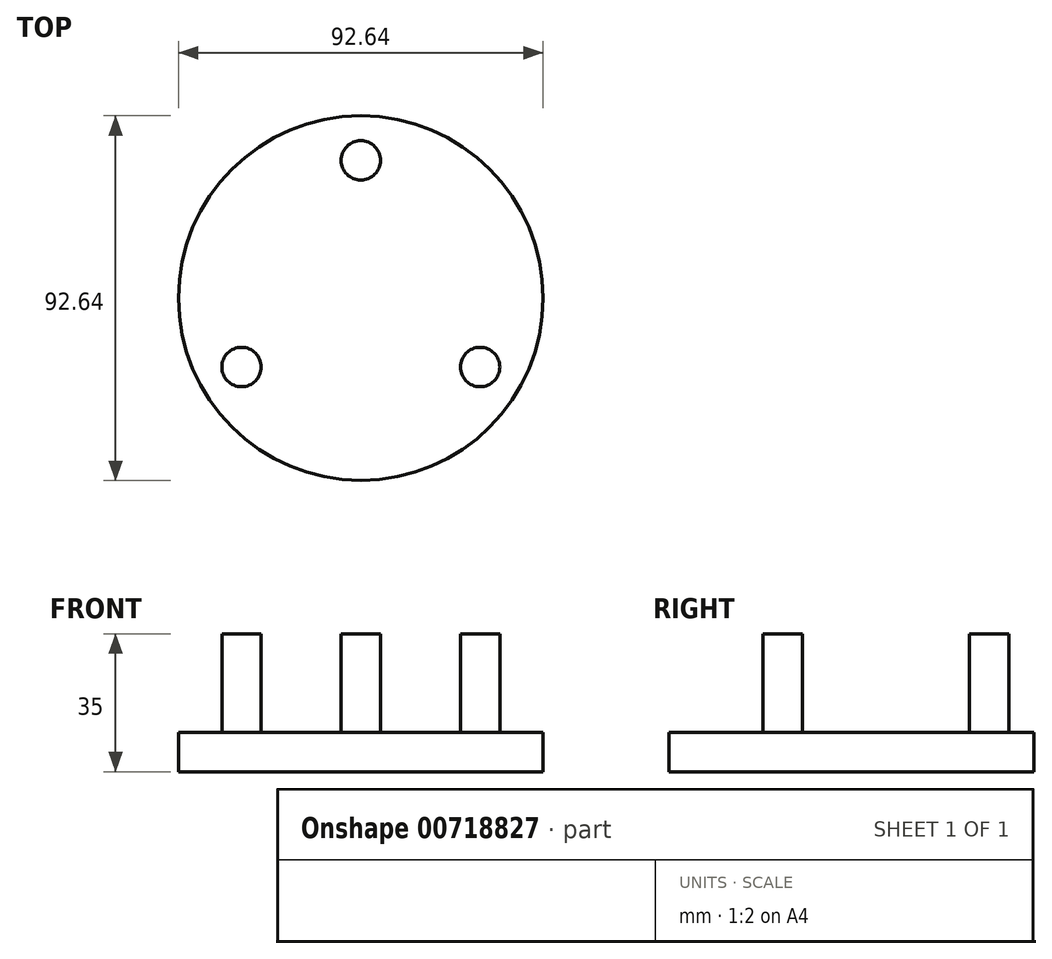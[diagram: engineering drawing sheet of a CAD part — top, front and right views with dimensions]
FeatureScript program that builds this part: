
annotation { "Feature Type Name" : "Feature", "Feature Type Description" : "" }
export const myFeature = defineFeature(function(context is Context, id is Id, definition is map)
    precondition{}
    {
        {
            var Q0;
            Q0=qCreatedBy(makeId("Top.planeOp"),FACE);
            var sketch = newSketch(context, id + "F0", { "sketchPlane" : qUnion([Q0])});
            skCircle(sketch, "E0", {"center": v(0, 0) * mm, "radius": 46.32 * mm});
            skSolve(sketch);
        }
        {
            var Q0;
            Q0=makeQuery(id+"F0.imprint","IMPRINT",FACE,{"disambiguationData":[TD([[makeQuery(id+"F0.imprint","IMPRINT",EDGE,{"derivedFrom":sQuery(id+"F0.wireOp",EDGE,"E0")}),1.0]])]});
            extrude(context, id + "F1", {"entities" : qUnion([Q0]), "endBound" : BoundingType.SYMMETRIC, "depth" : 10 * mm, "offsetDistance" : 25 * mm});
        }
        {
            var Q0;
            Q0=makeQuery(id+"F1.opExtrude","CAP_FACE",FACE,{"disambiguationData":[OSD([sQuery(id+"F0.wireOp",EDGE,"E0")])],"isStart":false});
            var sketch = newSketch(context, id + "F2", { "sketchPlane" : qUnion([Q0])});
            skCircle(sketch, "E1", {"center": v(0, 35) * mm, "radius": 5 * mm});
            skPoint(sketch, "E2.center", {"position": v(0, 0) * mm});
            skLineSegment(sketch, "E2.anchor1", {"start": v(0, 0) * mm, "end": v(0, 35) * mm, "construction": true});
            skLineSegment(sketch, "E2.anchor2", {"start": v(0, 0) * mm, "end": v(0, 35) * mm, "construction": true});
            skCircle(sketch, "E3.1.0", {"center": v(-30.31, -17.5) * mm, "radius": 5 * mm});
            skCircle(sketch, "E3.2.0", {"center": v(30.31, -17.5) * mm, "radius": 5 * mm});
            skSolve(sketch);
        }
        {
            var Q0;
            Q0 = qSketchRegion(id + "F2", true);
            extrude(context, id + "F3", {"entities" : qUnion([Q0]), "operationType" : NewBodyOperationType.ADD, "depth" : 25 * mm, "offsetDistance" : 25 * mm});
        }
    });
